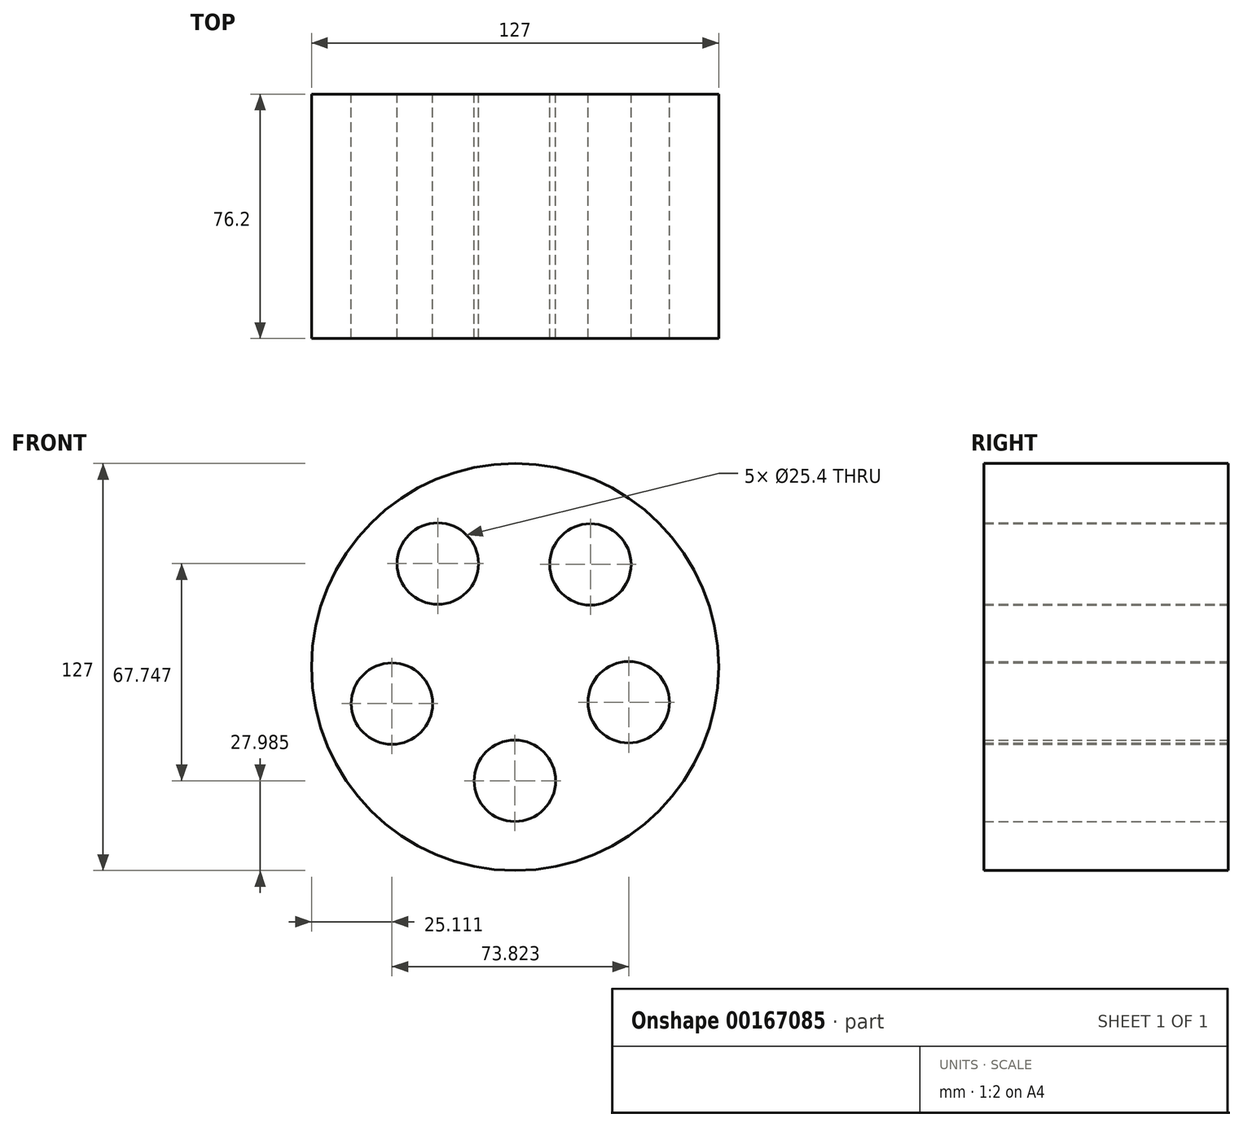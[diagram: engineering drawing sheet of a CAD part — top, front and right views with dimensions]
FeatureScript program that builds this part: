
annotation { "Feature Type Name" : "Feature", "Feature Type Description" : "" }
export const myFeature = defineFeature(function(context is Context, id is Id, definition is map)
    precondition{}
    {
        {
            var Q0;
            Q0=qCreatedBy(makeId("Front.planeOp"),FACE);
            var sketch = newSketch(context, id + "F0", { "sketchPlane" : qUnion([Q0])});
            skCircle(sketch, "E0", {"center": v(0, 0) * mm, "radius": 63.5 * mm});
            skCircle(sketch, "E1", {"center": v(-24.1, 32.23) * mm, "radius": 12.7 * mm});
            skCircle(sketch, "E2", {"center": v(23.49, 31.98) * mm, "radius": 12.7 * mm});
            skCircle(sketch, "E3", {"center": v(35.43, -11.02) * mm, "radius": 12.7 * mm});
            skCircle(sketch, "E4", {"center": v(-0.06, -35.52) * mm, "radius": 12.7 * mm});
            skCircle(sketch, "E5", {"center": v(-38.39, -11.46) * mm, "radius": 12.7 * mm});
            skSolve(sketch);
        }
        {
            var Q0;
            Q0=makeQuery(id+"F0.imprint","IMPRINT",FACE,{"disambiguationData":[TD([[makeQuery(id+"F0.imprint","IMPRINT",EDGE,{"derivedFrom":sQuery(id+"F0.wireOp",EDGE,"E0")}),1.0]])]});
            extrude(context, id + "F1", {"entities" : qUnion([Q0]), "depth" : 76.2 * mm});
        }
    });
